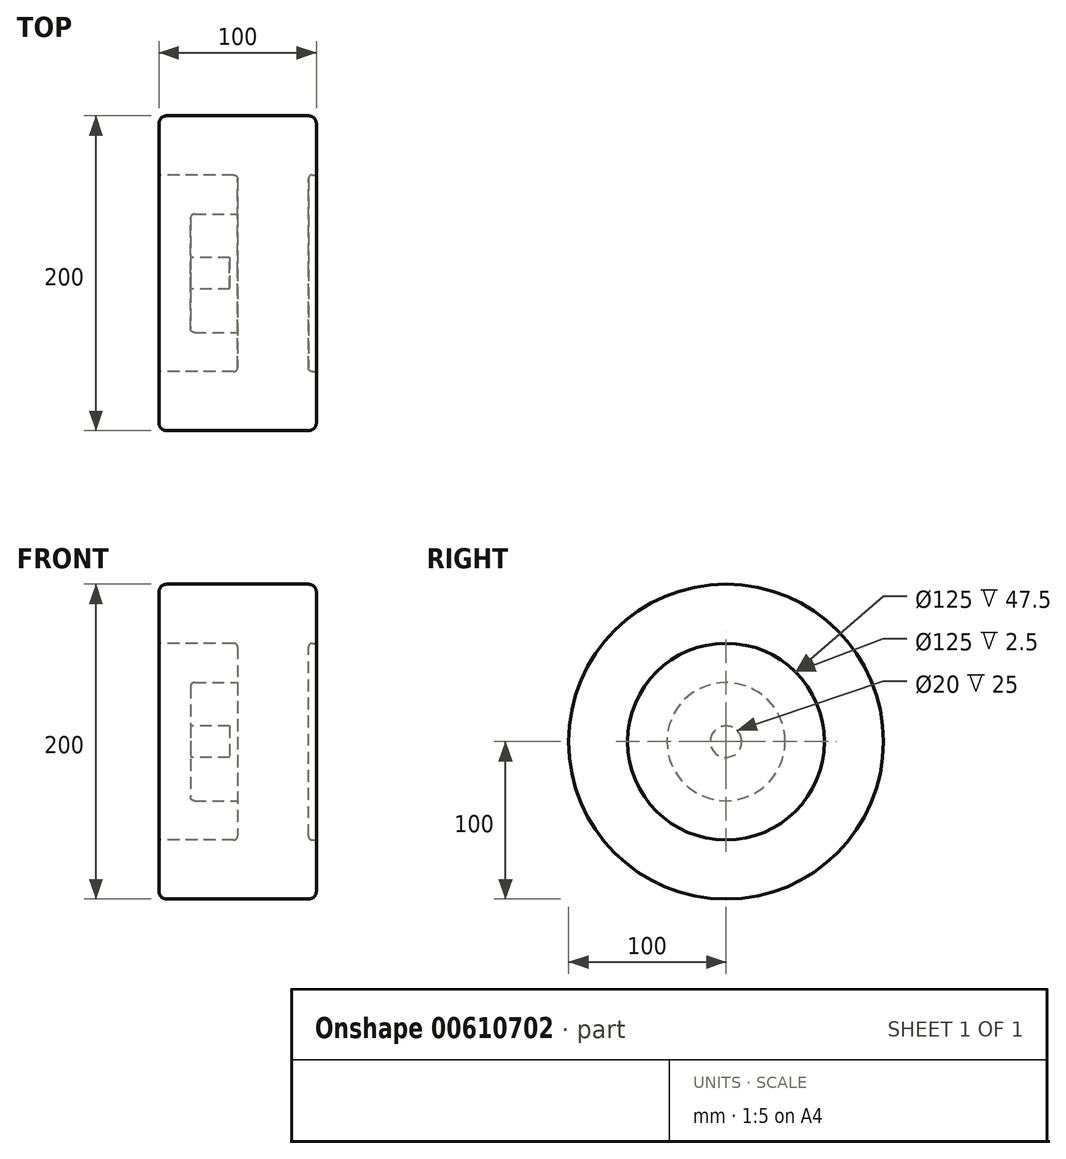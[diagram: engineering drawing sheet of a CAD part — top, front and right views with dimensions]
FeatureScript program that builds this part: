
annotation { "Feature Type Name" : "Feature", "Feature Type Description" : "" }
export const myFeature = defineFeature(function(context is Context, id is Id, definition is map)
    precondition{}
    {
        {
            var Q0;
            Q0=qCreatedBy(makeId("Right.planeOp"),FACE);
            var sketch = newSketch(context, id + "F0", { "sketchPlane" : qUnion([Q0])});
            skCircle(sketch, "E0", {"center": v(0, 0) * mm, "radius": 100 * mm});
            skSolve(sketch);
        }
        {
            var Q0;
            Q0 = qSketchRegion(id + "F0", true);
            extrude(context, id + "F1", {"entities" : qUnion([Q0]), "depth" : 100 * mm, "offsetDistance" : 25 * mm});
        }
        {
            var Q0;
            Q0=makeQuery(id+"F1.opExtrude","CAP_FACE",FACE,{"disambiguationData":[OSD([sQuery(id+"F0.wireOp",EDGE,"E0")])],"isStart":true});
            var sketch = newSketch(context, id + "F2", { "sketchPlane" : qUnion([Q0])});
            skCircle(sketch, "E1", {"center": v(0, 0) * mm, "radius": 62.5 * mm});
            skSolve(sketch);
        }
        {
            var Q0;
            Q0 = qSketchRegion(id + "F2", true);
            extrude(context, id + "F3", {"entities" : qUnion([Q0]), "operationType" : NewBodyOperationType.REMOVE, "oppositeDirection" : true, "depth" : 50 * mm, "offsetDistance" : 25 * mm});
        }
        {
            var Q0;
            Q0=makeQuery(id+"F1.opExtrude","CAP_FACE",FACE,{"disambiguationData":[OSD([sQuery(id+"F0.wireOp",EDGE,"E0")])],"isStart":false});
            var sketch = newSketch(context, id + "F4", { "sketchPlane" : qUnion([Q0])});
            skCircle(sketch, "E2", {"center": v(0, 0) * mm, "radius": 62.5 * mm});
            skSolve(sketch);
        }
        {
            var Q0;
            Q0=makeQuery(id+"F4.imprint","IMPRINT",FACE,{"disambiguationData":[TD([[makeQuery(id+"F4.imprint","IMPRINT",EDGE,{"derivedFrom":sQuery(id+"F4.wireOp",EDGE,"E2")}),1.0]])]});
            extrude(context, id + "F5", {"entities" : qUnion([Q0]), "operationType" : NewBodyOperationType.REMOVE, "oppositeDirection" : true, "depth" : 5 * mm, "offsetDistance" : 25 * mm});
        }
        {
            var Q0;
            Q0=makeQuery(id+"F1.opExtrude","CAP_EDGE",EDGE,{"disambiguationData":[OSD([sQuery(id+"F0.wireOp",EDGE,"E0")])],"isStart":true});
            var Q1;
            Q1=makeQuery(id+"F1.opExtrude","CAP_EDGE",EDGE,{"disambiguationData":[OSD([sQuery(id+"F0.wireOp",EDGE,"E0")])],"isStart":false});
            fillet(context, id + "F6", {"entities" : qUnion([Q0, Q1]), "radius" : 5 * mm, "tangentPropagation" : true, "allowEdgeOverflow" : false});
        }
        {
            var Q0;
            Q0=makeQuery(id+"F3.boolean.opBoolean","COPY",FACE,{"derivedFrom":makeQuery(id+"F3.opExtrude","CAP_FACE",FACE,{"disambiguationData":[OSD([sQuery(id+"F2.wireOp",EDGE,"E1")])],"isStart":false})});
            var sketch = newSketch(context, id + "F7", { "sketchPlane" : qUnion([Q0])});
            skCircle(sketch, "E3", {"center": v(0, 0) * mm, "radius": 37.5 * mm});
            skSolve(sketch);
        }
        {
            var Q0;
            Q0=makeQuery(id+"F7.imprint","IMPRINT",FACE,{"disambiguationData":[TD([[makeQuery(id+"F7.imprint","IMPRINT",EDGE,{"derivedFrom":sQuery(id+"F7.wireOp",EDGE,"E3")}),1.0]])]});
            extrude(context, id + "F8", {"entities" : qUnion([Q0]), "operationType" : NewBodyOperationType.ADD, "depth" : 30 * mm, "offsetDistance" : 25 * mm});
        }
        {
            var Q0;
            Q0=makeQuery(id+"F8.opExtrude","CAP_FACE",FACE,{"disambiguationData":[OSD([sQuery(id+"F7.wireOp",EDGE,"E3")])],"isStart":false});
            var sketch = newSketch(context, id + "F9", { "sketchPlane" : qUnion([Q0])});
            skCircle(sketch, "E4", {"center": v(0, 0) * mm, "radius": 10 * mm});
            skSolve(sketch);
        }
        {
            var Q0;
            Q0=makeQuery(id+"F9.imprint","IMPRINT",FACE,{"disambiguationData":[TD([[makeQuery(id+"F9.imprint","IMPRINT",EDGE,{"derivedFrom":sQuery(id+"F9.wireOp",EDGE,"E4")}),1.0]])]});
            extrude(context, id + "F10", {"entities" : qUnion([Q0]), "operationType" : NewBodyOperationType.REMOVE, "oppositeDirection" : true, "depth" : 25 * mm, "offsetDistance" : 25 * mm});
        }
        {
            var Q0;
            Q0=makeQuery(id+"F3.boolean.opBoolean","COPY",EDGE,{"derivedFrom":makeQuery(id+"F3.opExtrude","CAP_EDGE",EDGE,{"disambiguationData":[OSD([sQuery(id+"F2.wireOp",EDGE,"E1")])],"isStart":true})});
            var Q1;
            Q1=makeQuery(id+"F3.boolean.opBoolean","COPY",EDGE,{"derivedFrom":makeQuery(id+"F3.opExtrude","CAP_EDGE",EDGE,{"disambiguationData":[OSD([sQuery(id+"F2.wireOp",EDGE,"E1")])],"isStart":false})});
            var Q2;
            Q2=makeQuery(id+"F8.opExtrude","CAP_EDGE",EDGE,{"disambiguationData":[OSD([sQuery(id+"F7.wireOp",EDGE,"E3")])],"isStart":true});
            var Q3;
            Q3=makeQuery(id+"F8.opExtrude","CAP_EDGE",EDGE,{"disambiguationData":[OSD([sQuery(id+"F7.wireOp",EDGE,"E3")])],"isStart":false});
            var Q4;
            Q4=makeQuery(id+"F5.boolean.opBoolean","COPY",EDGE,{"derivedFrom":makeQuery(id+"F5.opExtrude","CAP_EDGE",EDGE,{"disambiguationData":[OSD([sQuery(id+"F4.wireOp",EDGE,"E2")])],"isStart":true})});
            var Q5;
            Q5=makeQuery(id+"F5.boolean.opBoolean","COPY",EDGE,{"derivedFrom":makeQuery(id+"F5.opExtrude","CAP_EDGE",EDGE,{"disambiguationData":[OSD([sQuery(id+"F4.wireOp",EDGE,"E2")])],"isStart":false})});
            fillet(context, id + "F11", {"entities" : qUnion([Q0, Q1, Q2, Q3, Q4, Q5]), "radius" : 2.5 * mm, "tangentPropagation" : true, "allowEdgeOverflow" : false});
        }
    });
